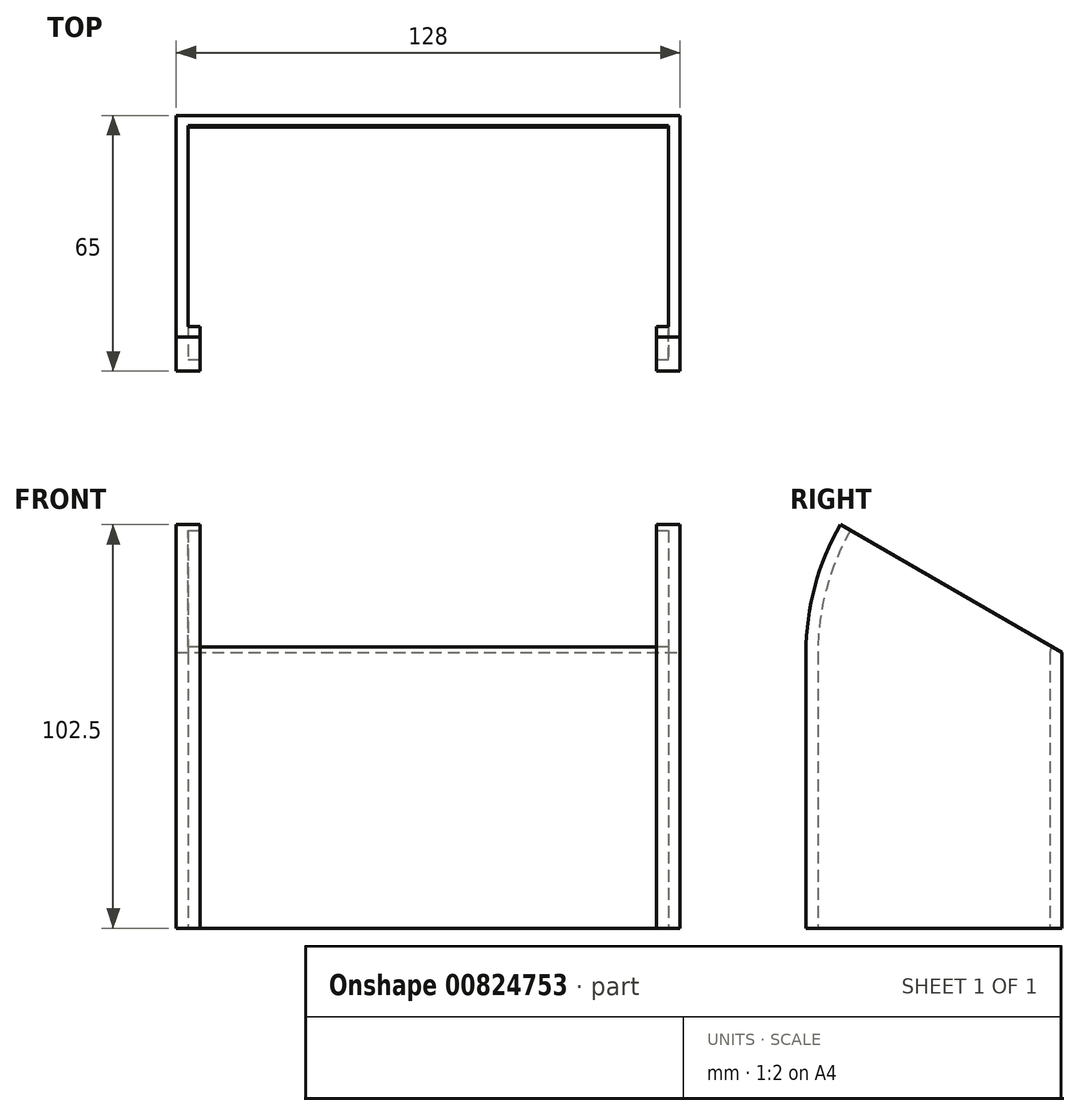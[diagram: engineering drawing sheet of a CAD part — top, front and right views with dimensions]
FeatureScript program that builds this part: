
annotation { "Feature Type Name" : "Feature", "Feature Type Description" : "" }
export const myFeature = defineFeature(function(context is Context, id is Id, definition is map)
    precondition{}
    {
        {
            var Q0;
            Q0=qCreatedBy(makeId("Top.planeOp"),FACE);
            var sketch = newSketch(context, id + "F0", { "sketchPlane" : qUnion([Q0])});
            skLineSegment(sketch, "E0", {"start": v(0, -32.22) * mm, "end": v(-6, -32.22) * mm});
            skLineSegment(sketch, "E1", {"start": v(-6, -32.22) * mm, "end": v(-6, 32.78) * mm});
            skLineSegment(sketch, "E2", {"start": v(-6, 32.78) * mm, "end": v(122, 32.78) * mm});
            skLineSegment(sketch, "E3", {"start": v(122, 32.78) * mm, "end": v(122, -32.22) * mm});
            skLineSegment(sketch, "E4", {"start": v(122, -32.22) * mm, "end": v(116, -32.22) * mm});
            skLineSegment(sketch, "E5", {"start": v(116, -32.22) * mm, "end": v(116, -29.22) * mm});
            skLineSegment(sketch, "E6", {"start": v(116, -29.22) * mm, "end": v(119, -29.22) * mm});
            skLineSegment(sketch, "E7", {"start": v(119, -29.22) * mm, "end": v(119, 29.78) * mm});
            skLineSegment(sketch, "E8", {"start": v(119, 29.78) * mm, "end": v(-3, 29.78) * mm});
            skLineSegment(sketch, "E9", {"start": v(-3, 29.78) * mm, "end": v(-3, -29.22) * mm});
            skLineSegment(sketch, "E10", {"start": v(-3, -29.22) * mm, "end": v(0, -29.22) * mm});
            skLineSegment(sketch, "E11", {"start": v(0, -29.22) * mm, "end": v(0, -32.22) * mm});
            skSolve(sketch);
        }
        {
            var Q0;
            Q0 = qSketchRegion(id + "F0", true);
            extrude(context, id + "F1", {"entities" : qUnion([Q0]), "depth" : 70 * mm, "offsetDistance" : 25 * mm});
        }
        {
            var Q0;
            Q0=makeQuery(id+"F1.opExtrude","CAP_FACE",FACE,{"disambiguationData":[OSD([sQuery(id+"F0.wireOp",EDGE,"E0"),sQuery(id+"F0.wireOp",EDGE,"E1"),sQuery(id+"F0.wireOp",EDGE,"E2"),sQuery(id+"F0.wireOp",EDGE,"E3"),sQuery(id+"F0.wireOp",EDGE,"E4"),sQuery(id+"F0.wireOp",EDGE,"E5"),sQuery(id+"F0.wireOp",EDGE,"E6"),sQuery(id+"F0.wireOp",EDGE,"E7"),sQuery(id+"F0.wireOp",EDGE,"E8"),sQuery(id+"F0.wireOp",EDGE,"E9"),sQuery(id+"F0.wireOp",EDGE,"E10"),sQuery(id+"F0.wireOp",EDGE,"E11")])],"isStart":false});
            var Q1;
            Q1=makeQuery(id+"F1.opExtrude","CAP_EDGE",EDGE,{"disambiguationData":[OSD([sQuery(id+"F0.wireOp",EDGE,"E2")])],"isStart":false});
            revolve(context, id + "F2", {"operationType" : NewBodyOperationType.ADD, "surfaceOperationType" : NewSurfaceOperationType.NEW, "entities" : qUnion([Q0]), "axis" : qUnion([Q1]), "revolveType" : RevolveType.ONE_DIRECTION, "oppositeDirection" : true, "angle" : 30 * degree});
        }
    });
